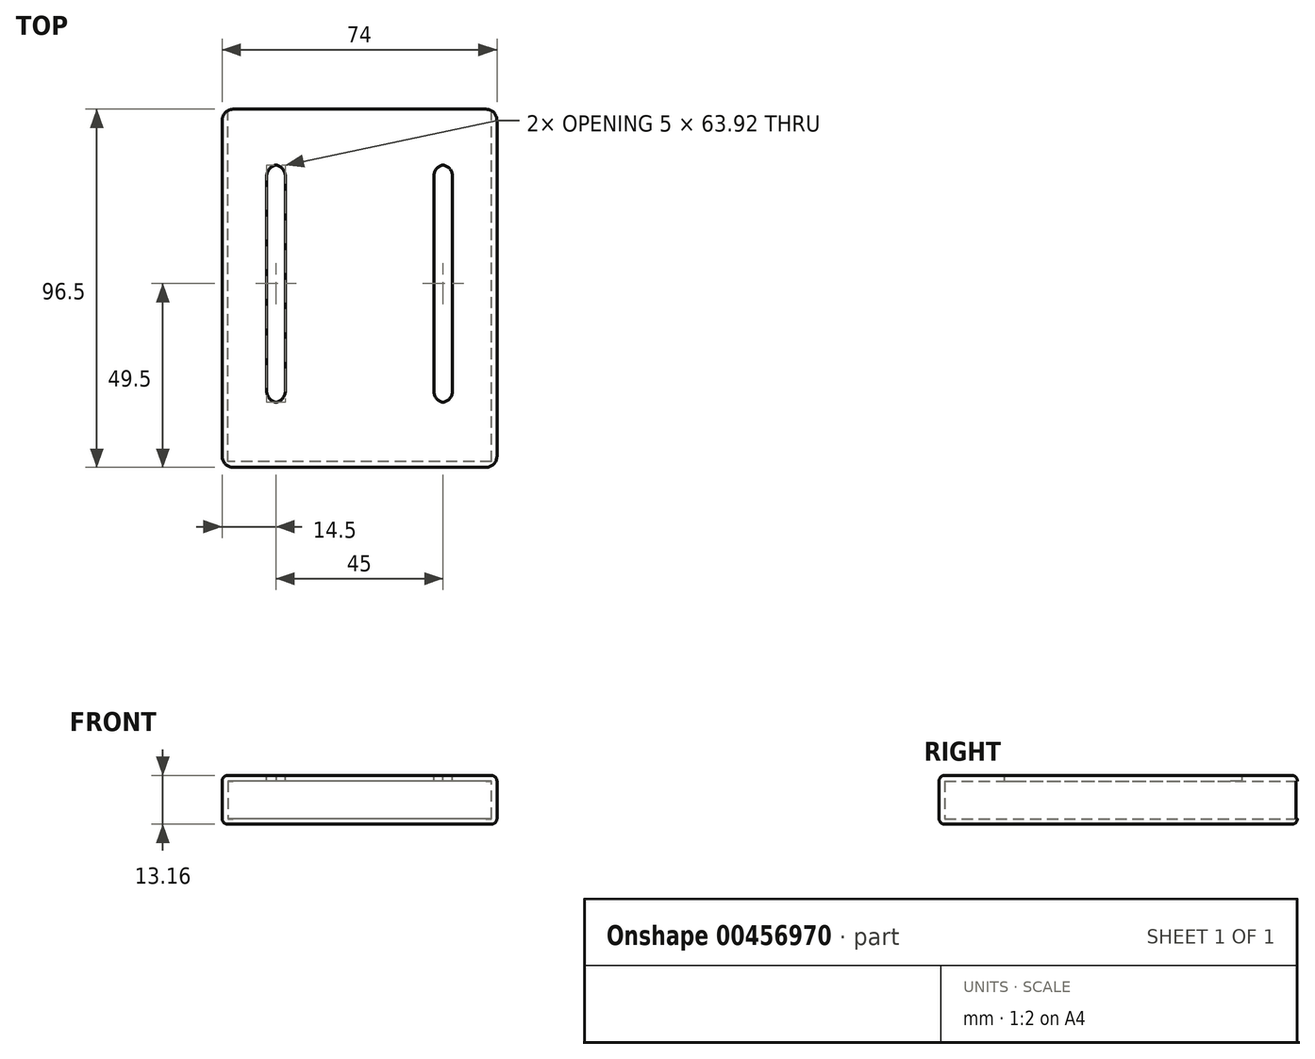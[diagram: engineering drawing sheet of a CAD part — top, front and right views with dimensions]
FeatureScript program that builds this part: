
annotation { "Feature Type Name" : "Feature", "Feature Type Description" : "" }
export const myFeature = defineFeature(function(context is Context, id is Id, definition is map)
    precondition{}
    {
        {
            var Q0;
            Q0=qCreatedBy(makeId("Front.planeOp"),FACE);
            var sketch = newSketch(context, id + "F0", { "sketchPlane" : qUnion([Q0])});
            skLineSegment(sketch, "E0.bottom", {"start": v(35.5, 5.08) * mm, "end": v(-35.5, 5.08) * mm});
            skLineSegment(sketch, "E0.top", {"start": v(35.5, -5.08) * mm, "end": v(-35.5, -5.08) * mm});
            skLineSegment(sketch, "E0.left", {"start": v(35.5, 5.08) * mm, "end": v(35.5, -5.07) * mm});
            skLineSegment(sketch, "E0.right", {"start": v(-35.5, 5.08) * mm, "end": v(-35.5, -5.08) * mm});
            skPoint(sketch, "E0.middle", {"position": v(0, 0) * mm});
            skLineSegment(sketch, "E1.bottom", {"start": v(37, 6.58) * mm, "end": v(-37, 6.58) * mm});
            skLineSegment(sketch, "E1.top", {"start": v(37, -6.58) * mm, "end": v(-37, -6.58) * mm});
            skLineSegment(sketch, "E1.left", {"start": v(37, 6.58) * mm, "end": v(37, -6.58) * mm});
            skLineSegment(sketch, "E1.right", {"start": v(-37, 6.58) * mm, "end": v(-37, -6.58) * mm});
            skSolve(sketch);
        }
        {
            var Q0;
            Q0=makeQuery(id+"F0.imprint","IMPRINT",FACE,{"disambiguationData":[TD([[makeQuery(id+"F0.imprint","IMPRINT",EDGE,{"derivedFrom":sQuery(id+"F0.wireOp",EDGE,"E0.bottom")}),1.0]])]});
            var Q1;
            Q1=makeQuery(id+"F0.imprint","IMPRINT",FACE,{"disambiguationData":[TD([[makeQuery(id+"F0.imprint","IMPRINT",EDGE,{"derivedFrom":sQuery(id+"F0.wireOp",EDGE,"E0.bottom")}),-1.0]])]});
            extrude(context, id + "F1", {"entities" : qUnion([Q0, Q1]), "depth" : 96.5 * mm});
        }
        {
            var Q0;
            Q0=makeQuery(id+"F0.imprint","IMPRINT",FACE,{"disambiguationData":[TD([[makeQuery(id+"F0.imprint","IMPRINT",EDGE,{"derivedFrom":sQuery(id+"F0.wireOp",EDGE,"E0.bottom")}),1.0]])]});
            extrude(context, id + "F2", {"entities" : qUnion([Q0]), "operationType" : NewBodyOperationType.REMOVE, "depth" : 95 * mm});
        }
        {
            var Q0;
            Q0=makeQuery(id+"F1.opExtrude","SWEPT_FACE",FACE,{"disambiguationData":[OSD([sQuery(id+"F0.wireOp",EDGE,"E1.bottom")])]});
            var sketch = newSketch(context, id + "F3", { "sketchPlane" : qUnion([Q0])});
            skLineSegment(sketch, "E2.bottom", {"start": v(20, -15) * mm, "end": v(25, -15) * mm});
            skLineSegment(sketch, "E2.top", {"start": v(20, -79) * mm, "end": v(25, -79) * mm});
            skLineSegment(sketch, "E2.left", {"start": v(20, -15) * mm, "end": v(20, -79) * mm});
            skLineSegment(sketch, "E2.right", {"start": v(25, -15) * mm, "end": v(25, -79) * mm});
            skPoint(sketch, "E2.middle", {"position": v(22.5, -47) * mm});
            skLineSegment(sketch, "E3.bottom", {"start": v(-20, -15) * mm, "end": v(-25, -15) * mm});
            skLineSegment(sketch, "E3.top", {"start": v(-20, -79) * mm, "end": v(-25, -79) * mm});
            skLineSegment(sketch, "E3.left", {"start": v(-20, -15) * mm, "end": v(-20, -79) * mm});
            skLineSegment(sketch, "E3.right", {"start": v(-25, -15) * mm, "end": v(-25, -79) * mm});
            skPoint(sketch, "E3.middle", {"position": v(-22.5, -47) * mm});
            skSolve(sketch);
        }
        {
            var Q0;
            Q0 = qSketchRegion(id + "F3", true);
            extrude(context, id + "F4", {"entities" : qUnion([Q0]), "operationType" : NewBodyOperationType.REMOVE, "oppositeDirection" : true, "depth" : 3 * mm});
        }
        {
            var Q0;
            Q0=makeQuery(id+"F1.opExtrude","CAP_EDGE",EDGE,{"disambiguationData":[OSD([sQuery(id+"F0.wireOp",EDGE,"E1.left")])],"isStart":false});
            var Q1;
            Q1=makeQuery(id+"F1.opExtrude","CAP_EDGE",EDGE,{"disambiguationData":[OSD([sQuery(id+"F0.wireOp",EDGE,"E1.right")])],"isStart":true});
            var Q2;
            Q2=makeQuery(id+"F1.opExtrude","CAP_EDGE",EDGE,{"disambiguationData":[OSD([sQuery(id+"F0.wireOp",EDGE,"E1.left")])],"isStart":true});
            var Q3;
            Q3=makeQuery(id+"F1.opExtrude","CAP_EDGE",EDGE,{"disambiguationData":[OSD([sQuery(id+"F0.wireOp",EDGE,"E1.right")])],"isStart":false});
            fillet(context, id + "F5", {"entities" : qUnion([Q0, Q1, Q2, Q3]), "radius" : 3 * mm, "tangentPropagation" : true, "allowEdgeOverflow" : false});
        }
        {
            var Q0;
            Q0=makeQuery(id+"F4.boolean.opBoolean","COPY",EDGE,{"derivedFrom":makeQuery(id+"F4.opExtrude","SWEPT_EDGE",EDGE,{"disambiguationData":[OSD([sQuery(id+"F3.wireOp",EDGE,"E2.top"),sQuery(id+"F3.wireOp",EDGE,"E2.right")])]})});
            var Q1;
            Q1=makeQuery(id+"F4.boolean.opBoolean","COPY",EDGE,{"derivedFrom":makeQuery(id+"F4.opExtrude","SWEPT_EDGE",EDGE,{"disambiguationData":[OSD([sQuery(id+"F3.wireOp",EDGE,"E2.bottom"),sQuery(id+"F3.wireOp",EDGE,"E2.left")])]})});
            var Q2;
            Q2=makeQuery(id+"F4.boolean.opBoolean","COPY",EDGE,{"derivedFrom":makeQuery(id+"F4.opExtrude","SWEPT_EDGE",EDGE,{"disambiguationData":[OSD([sQuery(id+"F3.wireOp",EDGE,"E2.bottom"),sQuery(id+"F3.wireOp",EDGE,"E2.right")])]})});
            var Q3;
            Q3=makeQuery(id+"F4.boolean.opBoolean","COPY",EDGE,{"derivedFrom":makeQuery(id+"F4.opExtrude","SWEPT_EDGE",EDGE,{"disambiguationData":[OSD([sQuery(id+"F3.wireOp",EDGE,"E2.top"),sQuery(id+"F3.wireOp",EDGE,"E2.left")])]})});
            var Q4;
            Q4=makeQuery(id+"F4.boolean.opBoolean","COPY",EDGE,{"derivedFrom":makeQuery(id+"F4.opExtrude","SWEPT_EDGE",EDGE,{"disambiguationData":[OSD([sQuery(id+"F3.wireOp",EDGE,"E3.top"),sQuery(id+"F3.wireOp",EDGE,"E3.left")])]})});
            var Q5;
            Q5=makeQuery(id+"F4.boolean.opBoolean","COPY",EDGE,{"derivedFrom":makeQuery(id+"F4.opExtrude","SWEPT_EDGE",EDGE,{"disambiguationData":[OSD([sQuery(id+"F3.wireOp",EDGE,"E3.bottom"),sQuery(id+"F3.wireOp",EDGE,"E3.right")])]})});
            var Q6;
            Q6=makeQuery(id+"F4.boolean.opBoolean","COPY",EDGE,{"derivedFrom":makeQuery(id+"F4.opExtrude","SWEPT_EDGE",EDGE,{"disambiguationData":[OSD([sQuery(id+"F3.wireOp",EDGE,"E3.top"),sQuery(id+"F3.wireOp",EDGE,"E3.right")])]})});
            var Q7;
            Q7=makeQuery(id+"F4.boolean.opBoolean","COPY",EDGE,{"derivedFrom":makeQuery(id+"F4.opExtrude","SWEPT_EDGE",EDGE,{"disambiguationData":[OSD([sQuery(id+"F3.wireOp",EDGE,"E3.bottom"),sQuery(id+"F3.wireOp",EDGE,"E3.left")])]})});
            fillet(context, id + "F6", {"entities" : qUnion([Q0, Q1, Q2, Q3, Q4, Q5, Q6, Q7]), "radius" : 3 * mm, "tangentPropagation" : true, "allowEdgeOverflow" : false});
        }
        {
            var Q0;
            Q0=makeQuery(id+"F1.opExtrude","CAP_EDGE",EDGE,{"disambiguationData":[OSD([sQuery(id+"F0.wireOp",EDGE,"E1.bottom")])],"isStart":false});
            var Q1;
            Q1=makeQuery(id+"F1.opExtrude","SWEPT_EDGE",EDGE,{"disambiguationData":[OSD([sQuery(id+"F0.wireOp",EDGE,"E1.bottom"),sQuery(id+"F0.wireOp",EDGE,"E1.left")])]});
            var Q2;
            Q2=makeQuery(id+"F1.opExtrude","SWEPT_EDGE",EDGE,{"disambiguationData":[OSD([sQuery(id+"F0.wireOp",EDGE,"E1.bottom"),sQuery(id+"F0.wireOp",EDGE,"E1.right")])]});
            var Q3;
            Q3=makeQuery(id+"F1.opExtrude","CAP_EDGE",EDGE,{"disambiguationData":[OSD([sQuery(id+"F0.wireOp",EDGE,"E1.top")])],"isStart":false});
            var Q4;
            Q4=makeQuery(id+"F1.opExtrude","SWEPT_EDGE",EDGE,{"disambiguationData":[OSD([sQuery(id+"F0.wireOp",EDGE,"E1.top"),sQuery(id+"F0.wireOp",EDGE,"E1.left")])]});
            var Q5;
            Q5=makeQuery(id+"F1.opExtrude","SWEPT_EDGE",EDGE,{"disambiguationData":[OSD([sQuery(id+"F0.wireOp",EDGE,"E1.top"),sQuery(id+"F0.wireOp",EDGE,"E1.right")])]});
            fillet(context, id + "F7", {"entities" : qUnion([Q0, Q1, Q2, Q3, Q4, Q5]), "radius" : 1.5 * mm, "tangentPropagation" : true, "allowEdgeOverflow" : false});
        }
    });
